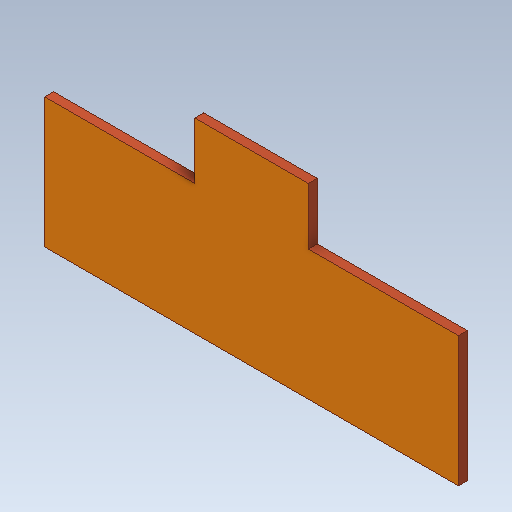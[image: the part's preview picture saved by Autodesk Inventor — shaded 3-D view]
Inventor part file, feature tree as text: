
AUTODESK INVENTOR PART (.ipt)
format: ipt  version: 2020 (Build 240168000, 168)  size: 107,520 bytes
history: native  units: mm
features: other x18, extrude x1, sketch x1
ambient origin geometry x8: Origin, YZ Plane, XZ Plane, XY Plane, X Axis, Y Axis, Z Axis, Center Point
bodies: Body1 (feature_tree)
feature tree (20):
  other  "Sólido1"
  extrude  "Extrusão1"  Depth=1.5mm
  sketch  "Esboço1"  dims[d3=1.5mm d4=0.0mm d6=3.0mm]
  other  "Referência1"
  other  "Referência8"
  other  "Referência9"
  other  "Referência10"
  other  "Referência11"
  other  "Referência12"
  other  "Referência13"
  other  "<userpath>\Desktop\rabo\3d\ela.iam"
  other  "ela.iam"
  other  "basesinha:1"
  other  "95658-EV3_Large_Motor v3:1"
  other  "10825-LtBluishGray:1"
  other  "TCS230-TCS3200:1"
  other  "Component2:1"
  other  "95658-EV3_Large_Motor v3_MIR:1"
  other  "99555-White_MIR:1"
  other  "10825-LtBluishGray_MIR:1"
